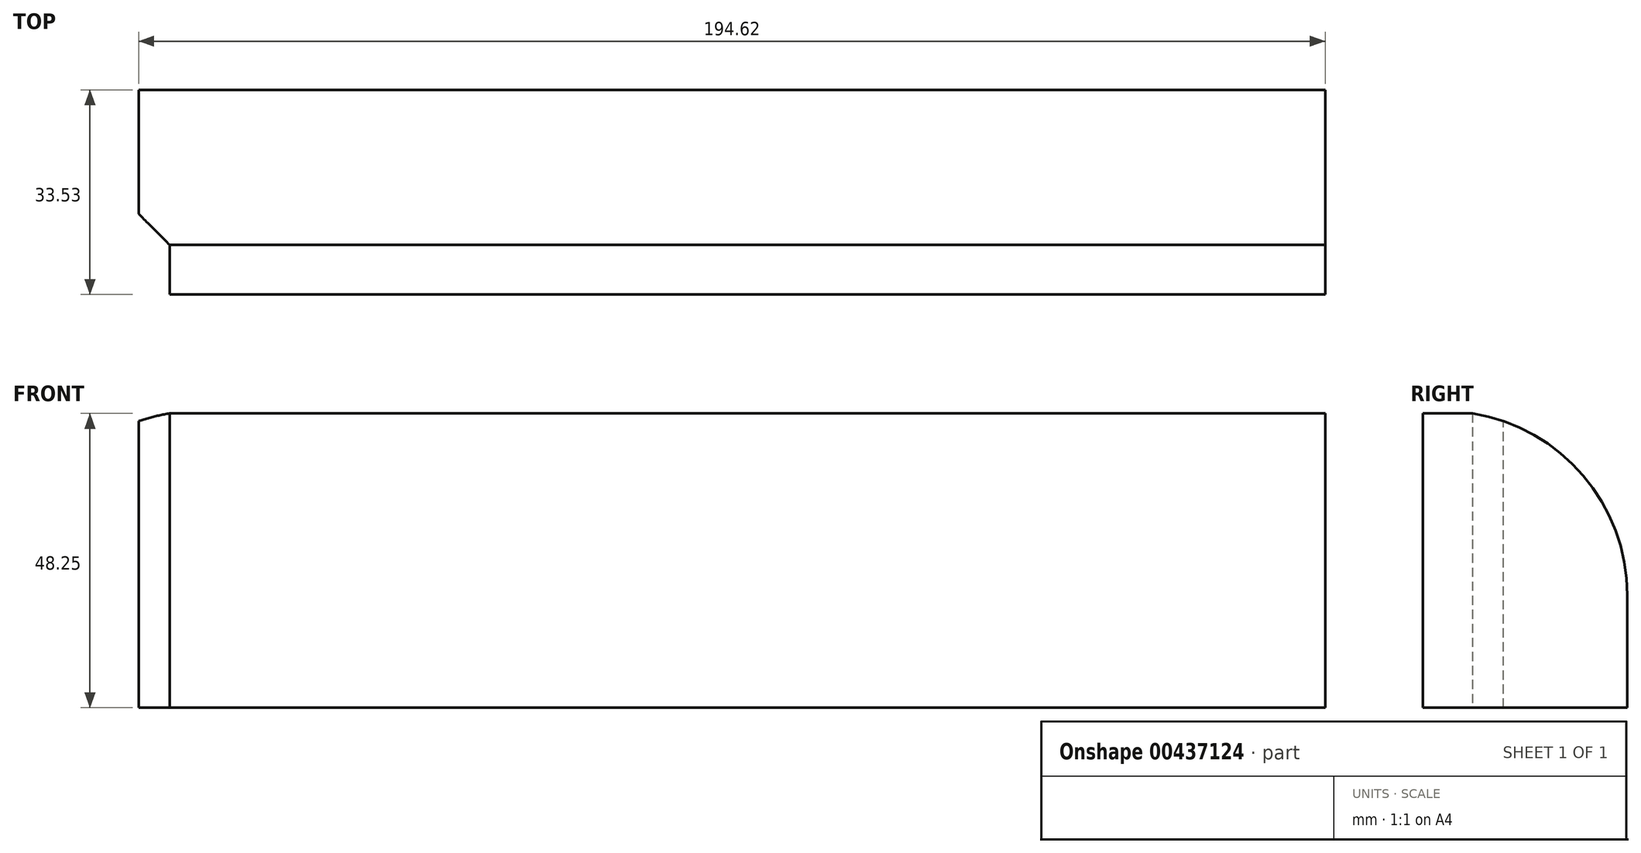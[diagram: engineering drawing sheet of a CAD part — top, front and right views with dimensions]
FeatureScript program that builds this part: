
annotation { "Feature Type Name" : "Feature", "Feature Type Description" : "" }
export const myFeature = defineFeature(function(context is Context, id is Id, definition is map)
    precondition{}
    {
        {
            var Q0;
            Q0=qCreatedBy(makeId("Front.planeOp"),FACE);
            var sketch = newSketch(context, id + "F0", { "sketchPlane" : qUnion([Q0])});
            skLineSegment(sketch, "E0.bottom", {"start": v(0, 60.3) * mm, "end": v(-194.62, 60.3) * mm});
            skLineSegment(sketch, "E0.top", {"start": v(0, 108.55) * mm, "end": v(-194.62, 108.55) * mm});
            skLineSegment(sketch, "E0.left", {"start": v(0, 60.3) * mm, "end": v(0, 108.55) * mm});
            skLineSegment(sketch, "E0.right", {"start": v(-194.62, 60.3) * mm, "end": v(-194.62, 108.55) * mm});
            skSolve(sketch);
        }
        {
            var Q0;
            Q0 = qSketchRegion(id + "F0", true);
            var Q1;
            Q1=makeQuery(id+"F0.imprint","IMPRINT",FACE,{"disambiguationData":[TD([[makeQuery(id+"F0.imprint","IMPRINT",EDGE,{"derivedFrom":sQuery(id+"F0.wireOp",EDGE,"E0.bottom")}),-1.0]])]});
            extrude(context, id + "F1", {"entities" : qUnion([Q0, Q1]), "depth" : 25.4 * mm});
        }
        {
            var Q0;
            Q0=makeQuery(id+"F1.opExtrude","CAP_EDGE",EDGE,{"disambiguationData":[OSD([sQuery(id+"F0.wireOp",EDGE,"E0.top")])],"isStart":true});
            fillet(context, id + "F2", {"entities" : qUnion([Q0]), "radius" : 30.16 * mm, "tangentPropagation" : true, "allowEdgeOverflow" : false});
        }
        {
            var Q0;
            Q0=makeQuery(id+"F1.opExtrude","CAP_EDGE",EDGE,{"disambiguationData":[OSD([sQuery(id+"F0.wireOp",EDGE,"E0.right")])],"isStart":false});
            chamfer(context, id + "F3", {"entities" : qUnion([Q0]), "width" : 5.08 * mm, "tangentPropagation" : true});
        }
        {
            var Q0;
            Q0=makeQuery(id+"F1.opExtrude","CAP_FACE",FACE,{"disambiguationData":[OSD([sQuery(id+"F0.wireOp",EDGE,"E0.bottom"),sQuery(id+"F0.wireOp",EDGE,"E0.top"),sQuery(id+"F0.wireOp",EDGE,"E0.left"),sQuery(id+"F0.wireOp",EDGE,"E0.right")])],"isStart":false});
            var sketch = newSketch(context, id + "F4", { "sketchPlane" : qUnion([Q0])});
            skSolve(sketch);
        }
        {
            var Q0;
            Q0 = qSketchRegion(id + "F4", true);
            var Q1;
            {var subQ0=sQuery(id+"F0.wireOp",EDGE,"E0.left");Q1=makeQuery(id+"F4.imprint","IMPRINT",FACE,{"disambiguationData":[TD([[makeQuery(id+"F4.imprint","IMPRINT",EDGE,{"derivedFrom":makeQuery(id+"F1.opExtrude","CAP_EDGE",EDGE,{"disambiguationData":[OSD([subQ0])],"isStart":false})}),1.0]])]});}
            extrude(context, id + "F5", {"entities" : qUnion([Q0, Q1]), "operationType" : NewBodyOperationType.ADD, "depth" : 8.13 * mm});
        }
    });
